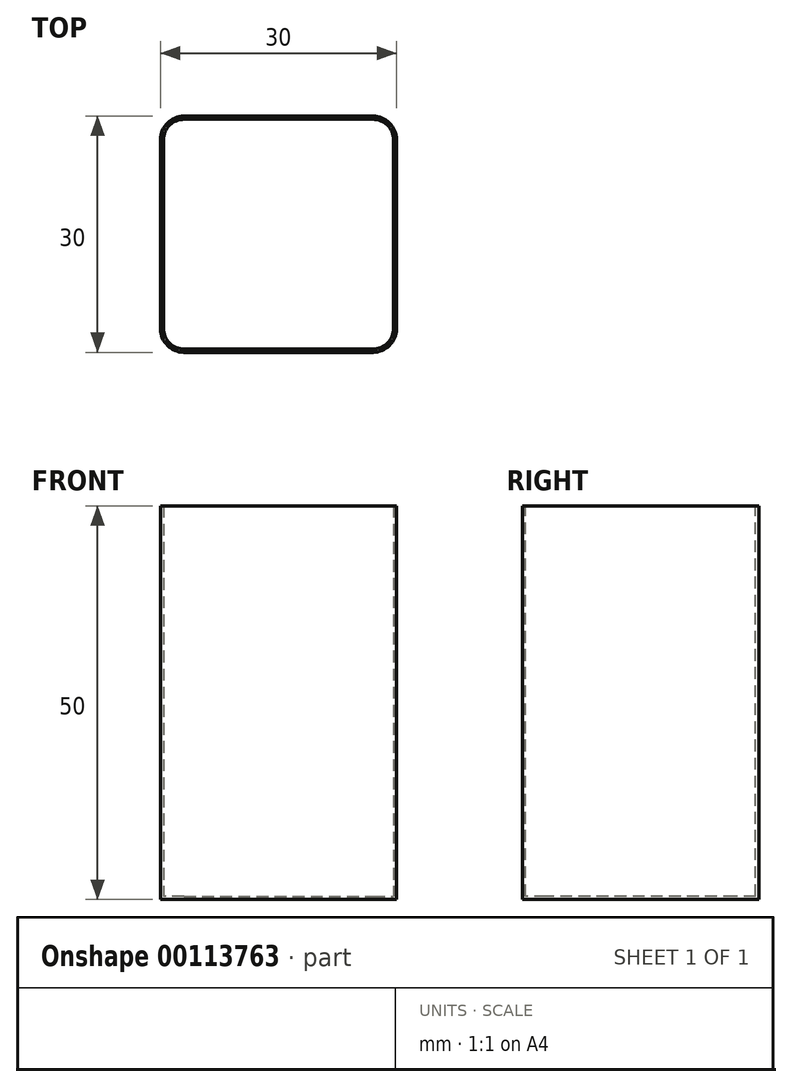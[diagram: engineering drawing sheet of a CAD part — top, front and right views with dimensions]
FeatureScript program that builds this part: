
annotation { "Feature Type Name" : "Feature", "Feature Type Description" : "" }
export const myFeature = defineFeature(function(context is Context, id is Id, definition is map)
    precondition{}
    {
        {
            var Q0;
            Q0=qCreatedBy(makeId("Top.planeOp"),FACE);
            var sketch = newSketch(context, id + "F0", { "sketchPlane" : qUnion([Q0])});
            skLineSegment(sketch, "E0.bottom", {"start": v(-27, 30) * mm, "end": v(-3, 30) * mm});
            skLineSegment(sketch, "E0.top", {"start": v(-27, 0) * mm, "end": v(-3, 0) * mm});
            skLineSegment(sketch, "E0.left", {"start": v(-30, 27) * mm, "end": v(-30, 3) * mm});
            skLineSegment(sketch, "E0.right", {"start": v(0, 27) * mm, "end": v(0, 3) * mm});
            skPoint(sketch, "E1.visualSharp", {"position": v(-0.4, 29.6) * mm});
            skPoint(sketch, "E2.visualSharp", {"position": v(0, 30) * mm});
            skArc(sketch, "E2.filletArc", {"start": v(0, 27) * mm, "mid": v(-0.88, 29.12) * mm, "end": v(-3, 30) * mm});
            skPoint(sketch, "E3.visualSharp", {"position": v(-29.6, 29.6) * mm});
            skPoint(sketch, "E4.visualSharp", {"position": v(-30, 30) * mm});
            skArc(sketch, "E4.filletArc", {"start": v(-27, 30) * mm, "mid": v(-29.12, 29.12) * mm, "end": v(-30, 27) * mm});
            skPoint(sketch, "E5.visualSharp", {"position": v(-29.6, 0.4) * mm});
            skPoint(sketch, "E6.visualSharp", {"position": v(-0.4, 0.4) * mm});
            skPoint(sketch, "E7.visualSharp", {"position": v(-30, 0) * mm});
            skArc(sketch, "E7.filletArc", {"start": v(-30, 3) * mm, "mid": v(-29.12, 0.88) * mm, "end": v(-27, 0) * mm});
            skPoint(sketch, "E8.visualSharp", {"position": v(0, 0) * mm});
            skArc(sketch, "E8.filletArc", {"start": v(-3, 0) * mm, "mid": v(-0.88, 0.88) * mm, "end": v(0, 3) * mm});
            skSolve(sketch);
        }
        {
            var Q0;
            Q0=makeQuery(id+"F0.imprint","IMPRINT",FACE,{"disambiguationData":[TD([[makeQuery(id+"F0.imprint","IMPRINT",EDGE,{"derivedFrom":sQuery(id+"F0.wireOp",EDGE,"E0.bottom")}),-1.0]])]});
            extrude(context, id + "F1", {"entities" : qUnion([Q0]), "depth" : 50 * mm});
        }
        {
            var Q0;
            Q0=makeQuery(id+"F1.opExtrude","CAP_FACE",FACE,{"disambiguationData":[OSD([sQuery(id+"F0.wireOp",EDGE,"E0.bottom"),sQuery(id+"F0.wireOp",EDGE,"E0.top"),sQuery(id+"F0.wireOp",EDGE,"E0.left"),sQuery(id+"F0.wireOp",EDGE,"E0.right"),sQuery(id+"F0.wireOp",EDGE,"E2.filletArc"),sQuery(id+"F0.wireOp",EDGE,"E4.filletArc"),sQuery(id+"F0.wireOp",EDGE,"E7.filletArc"),sQuery(id+"F0.wireOp",EDGE,"E8.filletArc")])],"isStart":false});
            shell(context, id + "F2", {"entities" : qUnion([Q0]), "thickness" : 0.4 * mm});
        }
    });
